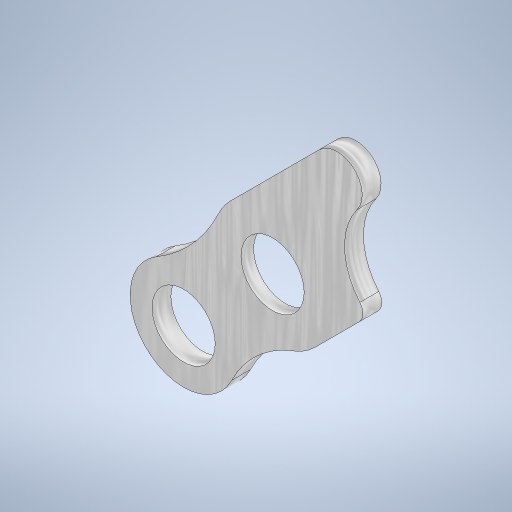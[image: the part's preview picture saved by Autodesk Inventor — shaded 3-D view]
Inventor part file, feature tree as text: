
AUTODESK INVENTOR PART (.ipt)
format: ipt  version: 2023 (Build 270158000, 158)  size: 307,200 bytes
history: native  units: mm
features: extrude x2, sketch x1
ambient origin geometry x8: Origin, YZ Plane, XZ Plane, XY Plane, X Axis, Y Axis, Z Axis, Center Point
bodies: Solid1 (feature_tree)
feature tree (3):
  sketch  "Sketch1"  dims[d31=3.0mm d32=0.0mm d33=10.05mm d34=20.0mm d35=10.05mm d36=19.0mm d37=17.0mm d38=4.0mm d39=2.0mm d40=10.0mm d41=20.0mm d42=10.0mm d43=15.0mm d44=15.0mm d45=25.0mm d46=18.0mm d47=45.0deg d48=2.0mm d49=0.0mm]
  extrude  "Extrusion1"  Depth=2.0mm TaperAngle=0.0deg
  extrude  "Extrusion2"  [1 undecoded]
note: 1 required parameter value undecoded (feature->parameter linkage not recoverable at this tier; creation-order binding heuristic only, values carry confidence <= 0.55)
